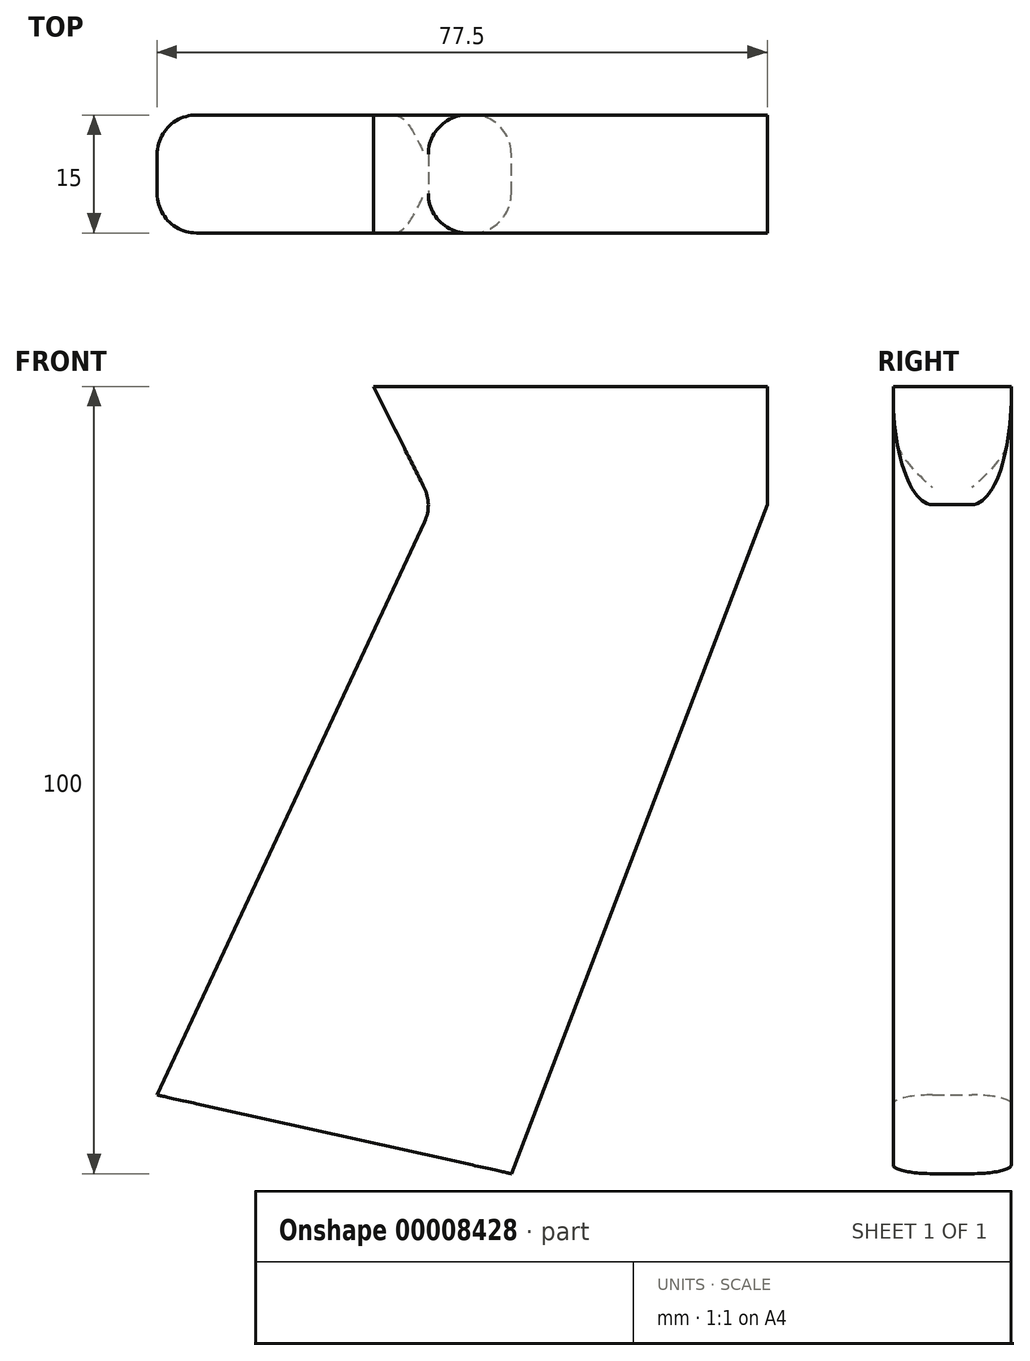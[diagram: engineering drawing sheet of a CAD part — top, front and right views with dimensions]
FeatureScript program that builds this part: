
annotation { "Feature Type Name" : "Feature", "Feature Type Description" : "" }
export const myFeature = defineFeature(function(context is Context, id is Id, definition is map)
    precondition{}
    {
        {
            var Q0;
            Q0=qCreatedBy(makeId("Front.planeOp"),FACE);
            var sketch = newSketch(context, id + "F0", { "sketchPlane" : qUnion([Q0])});
            skLineSegment(sketch, "E0", {"start": v(0, 0) * mm, "end": v(-50, 0) * mm});
            skLineSegment(sketch, "E1", {"start": v(-50, 0) * mm, "end": v(-42.5, -15) * mm});
            skLineSegment(sketch, "E2", {"start": v(-42.5, -15) * mm, "end": v(-77.5, -90) * mm});
            skLineSegment(sketch, "E3", {"start": v(-77.5, -90) * mm, "end": v(-32.5, -100) * mm});
            skLineSegment(sketch, "E4", {"start": v(-32.5, -100) * mm, "end": v(0, -15) * mm});
            skLineSegment(sketch, "E5", {"start": v(0, -15) * mm, "end": v(0, 0) * mm});
            skSolve(sketch);
        }
        {
            var Q0;
            Q0 = qSketchRegion(id + "F0", true);
            extrude(context, id + "F1", {"entities" : qUnion([Q0]), "depth" : 15 * mm});
        }
        {
            var Q0;
            Q0=makeQuery(id+"F1.opExtrude","CAP_EDGE",EDGE,{"disambiguationData":[OSD([sQuery(id+"F0.wireOp",EDGE,"E2")])],"isStart":false});
            var Q1;
            Q1=makeQuery(id+"F1.opExtrude","CAP_EDGE",EDGE,{"disambiguationData":[OSD([sQuery(id+"F0.wireOp",EDGE,"E2")])],"isStart":true});
            var Q2;
            Q2=makeQuery(id+"F1.opExtrude","CAP_EDGE",EDGE,{"disambiguationData":[OSD([sQuery(id+"F0.wireOp",EDGE,"E4")])],"isStart":false});
            var Q3;
            Q3=makeQuery(id+"F1.opExtrude","CAP_EDGE",EDGE,{"disambiguationData":[OSD([sQuery(id+"F0.wireOp",EDGE,"E4")])],"isStart":true});
            var Q4;
            Q4=makeQuery(id+"F1.opExtrude","SWEPT_EDGE",EDGE,{"disambiguationData":[OSD([sQuery(id+"F0.wireOp",EDGE,"E1"),sQuery(id+"F0.wireOp",EDGE,"E2")])]});
            fillet(context, id + "F2", {"entities" : qUnion([Q0, Q1, Q2, Q3, Q4]), "radius" : 5 * mm, "tangentPropagation" : true, "allowEdgeOverflow" : false});
        }
    });
